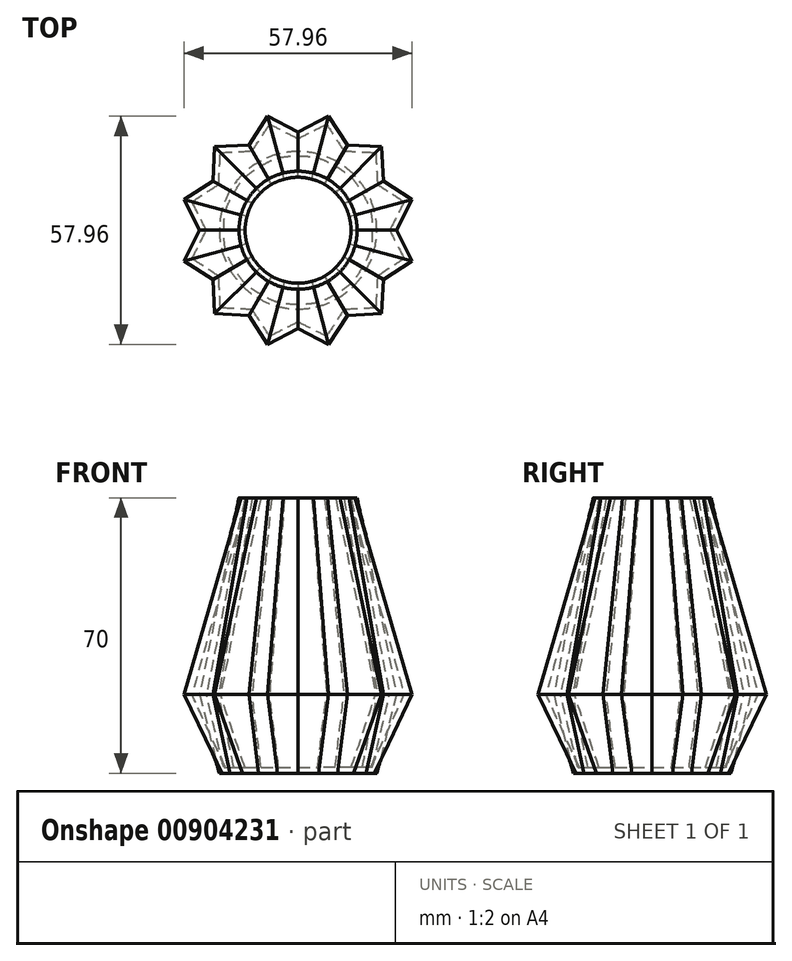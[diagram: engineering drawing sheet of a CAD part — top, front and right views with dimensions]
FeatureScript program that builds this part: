
annotation { "Feature Type Name" : "Feature", "Feature Type Description" : "" }
export const myFeature = defineFeature(function(context is Context, id is Id, definition is map)
    precondition{}
    {
        {
            var Q0;
            Q0=qCreatedBy(makeId("Top.planeOp"),FACE);
            var sketch = newSketch(context, id + "F0", { "sketchPlane" : qUnion([Q0])});
            skCircle(sketch, "E0", {"center": v(0, 0) * mm, "radius": 20 * mm});
            skSolve(sketch);
        }
        {
            var Q0;
            Q0=qCreatedBy(makeId("Top.planeOp"),FACE);
            cPlane(context, id + "F1", {"entities" : qUnion([Q0]), "cplaneType" : CPlaneType.OFFSET, "offset" : 20 * mm, "width" : 150 * mm, "height" : 150 * mm});
        }
        {
            var Q0;
            Q0=qCreatedBy(id+"F1.planeOp",FACE);
            var sketch = newSketch(context, id + "F2", { "sketchPlane" : qUnion([Q0])});
            skLineSegment(sketch, "E1", {"start": v(0, 0) * mm, "end": v(0, 25) * mm, "construction": true});
            skLineSegment(sketch, "E2", {"start": v(12.5, 21.65) * mm, "end": v(0, 0) * mm, "construction": true});
            skLineSegment(sketch, "E3", {"start": v(0, 0) * mm, "end": v(7.76, 28.98) * mm, "construction": true});
            skLineSegment(sketch, "E4", {"start": v(7.76, 28.98) * mm, "end": v(12.5, 21.65) * mm});
            skLineSegment(sketch, "E5", {"start": v(7.76, 28.98) * mm, "end": v(0, 25) * mm});
            skLineSegment(sketch, "E6.1.0", {"start": v(-7.76, 28.98) * mm, "end": v(0, 25) * mm});
            skLineSegment(sketch, "E6.1.1", {"start": v(-7.76, 28.98) * mm, "end": v(-12.5, 21.65) * mm});
            skLineSegment(sketch, "E6.2.0", {"start": v(-21.21, 21.21) * mm, "end": v(-12.5, 21.65) * mm});
            skLineSegment(sketch, "E6.2.1", {"start": v(-21.21, 21.21) * mm, "end": v(-21.65, 12.5) * mm});
            skLineSegment(sketch, "E6.3.0", {"start": v(-28.98, 7.76) * mm, "end": v(-21.65, 12.5) * mm});
            skLineSegment(sketch, "E6.3.1", {"start": v(-28.98, 7.76) * mm, "end": v(-25, 0) * mm});
            skLineSegment(sketch, "E6.4.0", {"start": v(-28.98, -7.76) * mm, "end": v(-25, 0) * mm});
            skLineSegment(sketch, "E6.4.1", {"start": v(-28.98, -7.76) * mm, "end": v(-21.65, -12.5) * mm});
            skLineSegment(sketch, "E6.5.0", {"start": v(-21.21, -21.21) * mm, "end": v(-21.65, -12.5) * mm});
            skLineSegment(sketch, "E6.5.1", {"start": v(-21.21, -21.21) * mm, "end": v(-12.5, -21.65) * mm});
            skLineSegment(sketch, "E6.6.0", {"start": v(-7.76, -28.98) * mm, "end": v(-12.5, -21.65) * mm});
            skLineSegment(sketch, "E6.6.1", {"start": v(-7.76, -28.98) * mm, "end": v(0, -25) * mm});
            skLineSegment(sketch, "E6.7.0", {"start": v(7.76, -28.98) * mm, "end": v(0, -25) * mm});
            skLineSegment(sketch, "E6.7.1", {"start": v(7.76, -28.98) * mm, "end": v(12.5, -21.65) * mm});
            skLineSegment(sketch, "E6.8.0", {"start": v(21.21, -21.21) * mm, "end": v(12.5, -21.65) * mm});
            skLineSegment(sketch, "E6.8.1", {"start": v(21.21, -21.21) * mm, "end": v(21.65, -12.5) * mm});
            skLineSegment(sketch, "E6.9.0", {"start": v(28.98, -7.76) * mm, "end": v(21.65, -12.5) * mm});
            skLineSegment(sketch, "E6.9.1", {"start": v(28.98, -7.76) * mm, "end": v(25, 0) * mm});
            skLineSegment(sketch, "E6.10.0", {"start": v(28.98, 7.76) * mm, "end": v(25, 0) * mm});
            skLineSegment(sketch, "E6.10.1", {"start": v(28.98, 7.76) * mm, "end": v(21.65, 12.5) * mm});
            skLineSegment(sketch, "E6.11.0", {"start": v(21.21, 21.21) * mm, "end": v(21.65, 12.5) * mm});
            skLineSegment(sketch, "E6.11.1", {"start": v(21.21, 21.21) * mm, "end": v(12.5, 21.65) * mm});
            skPoint(sketch, "E6.center", {"position": v(0, 0) * mm});
            skSolve(sketch);
        }
        {
            var Q0;
            Q0=makeQuery(id+"F2.imprint","IMPRINT",FACE,{"disambiguationData":[TD([[makeQuery(id+"F2.imprint","IMPRINT",EDGE,{"derivedFrom":sQuery(id+"F2.wireOp",EDGE,"E4")}),-1.0]])]});
            var Q1;
            Q1=makeQuery(id+"F0.imprint","IMPRINT",FACE,{"disambiguationData":[TD([[makeQuery(id+"F0.imprint","IMPRINT",EDGE,{"derivedFrom":sQuery(id+"F0.wireOp",EDGE,"E0")}),1.0]])]});
            loft(context, id + "F3", {"sheetProfilesArray" : [{ "sheetProfileEntities" : qUnion([Q0]) }, { "sheetProfileEntities" : qUnion([Q1]) }]});
        }
        {
            var Q0;
            Q0=makeQuery(id+"F3.opLoft","CAP_FACE",FACE,{"disambiguationData":[OSD([makeQuery(id+"F2.imprint","IMPRINT",FACE,{"disambiguationData":[TD([[makeQuery(id+"F2.imprint","IMPRINT",EDGE,{"derivedFrom":sQuery(id+"F2.wireOp",EDGE,"E4")}),-1.0]])]})])],"isStart":true});
            cPlane(context, id + "F4", {"entities" : qUnion([Q0]), "cplaneType" : CPlaneType.OFFSET, "offset" : 50 * mm, "width" : 150 * mm, "height" : 150 * mm});
        }
        {
            var Q0;
            Q0=qCreatedBy(id+"F4.planeOp",FACE);
            var sketch = newSketch(context, id + "F5", { "sketchPlane" : qUnion([Q0])});
            skCircle(sketch, "E7", {"center": v(0, 0) * mm, "radius": 15 * mm});
            skSolve(sketch);
        }
        {
            var Q1;
            Q1=makeQuery(id+"F5.imprint","IMPRINT",FACE,{"disambiguationData":[TD([[makeQuery(id+"F5.imprint","IMPRINT",EDGE,{"derivedFrom":sQuery(id+"F5.wireOp",EDGE,"E7")}),1.0]])]});
            var Q2;
            Q2=makeQuery(id+"F3.opLoft","CAP_FACE",FACE,{"disambiguationData":[OSD([makeQuery(id+"F2.imprint","IMPRINT",FACE,{"disambiguationData":[TD([[makeQuery(id+"F2.imprint","IMPRINT",EDGE,{"derivedFrom":sQuery(id+"F2.wireOp",EDGE,"E4")}),-1.0]])]})])],"isStart":true});
            loft(context, id + "F6", {"operationType" : NewBodyOperationType.ADD, "sheetProfilesArray" : [{ "sheetProfileEntities" : qUnion([Q1]) }, { "sheetProfileEntities" : qUnion([Q2]) }]});
        }
        {
            var Q0;
            Q0=makeQuery(id+"F6.opLoft","CAP_FACE",FACE,{"disambiguationData":[OSD([makeQuery(id+"F5.imprint","IMPRINT",FACE,{"disambiguationData":[TD([[makeQuery(id+"F5.imprint","IMPRINT",EDGE,{"derivedFrom":sQuery(id+"F5.wireOp",EDGE,"E7")}),1.0]])]})])],"isStart":true});
            shell(context, id + "F7", {"entities" : qUnion([Q0]), "thickness" : 1.5 * mm});
        }
    });
